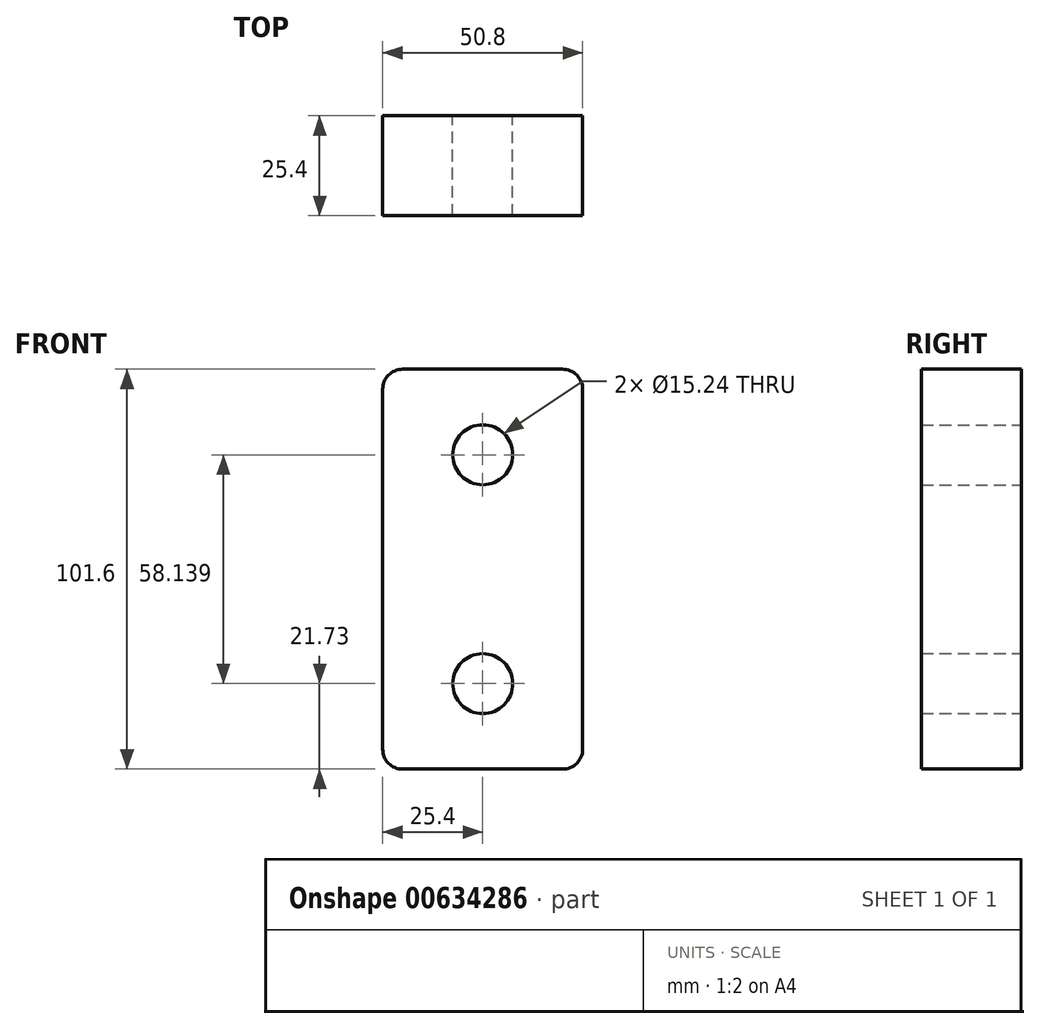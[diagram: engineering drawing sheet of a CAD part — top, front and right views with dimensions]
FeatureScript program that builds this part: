
annotation { "Feature Type Name" : "Feature", "Feature Type Description" : "" }
export const myFeature = defineFeature(function(context is Context, id is Id, definition is map)
    precondition{}
    {
        {
            var Q0;
            Q0=qCreatedBy(makeId("Front.planeOp"),FACE);
            var sketch = newSketch(context, id + "F0", { "sketchPlane" : qUnion([Q0])});
            skLineSegment(sketch, "E0.bottom", {"start": v(25.4, -50.8) * mm, "end": v(-25.4, -50.8) * mm});
            skLineSegment(sketch, "E0.top", {"start": v(25.4, 50.8) * mm, "end": v(-25.4, 50.8) * mm});
            skLineSegment(sketch, "E0.left", {"start": v(25.4, -50.8) * mm, "end": v(25.4, 50.8) * mm});
            skLineSegment(sketch, "E0.right", {"start": v(-25.4, -50.8) * mm, "end": v(-25.4, 50.8) * mm});
            skPoint(sketch, "E0.middle", {"position": v(0, 0) * mm});
            skCircle(sketch, "E1", {"center": v(0, -29.07) * mm, "radius": 7.62 * mm});
            skCircle(sketch, "E2.MirrorC", {"center": v(0, 29.07) * mm, "radius": 7.62 * mm});
            skSolve(sketch);
        }
        {
            var Q0;
            Q0=makeQuery(id+"F0.imprint","IMPRINT",FACE,{"disambiguationData":[TD([[makeQuery(id+"F0.imprint","IMPRINT",EDGE,{"derivedFrom":sQuery(id+"F0.wireOp",EDGE,"E0.bottom")}),-1.0]])]});
            extrude(context, id + "F1", {"entities" : qUnion([Q0]), "endBound" : BoundingType.SYMMETRIC, "depth" : 25.4 * mm, "offsetDistance" : 25.4 * mm});
        }
        {
            var Q0;
            Q0=makeQuery(id+"F1.opExtrude","SWEPT_EDGE",EDGE,{"disambiguationData":[OSD([sQuery(id+"F0.wireOp",EDGE,"E0.top"),sQuery(id+"F0.wireOp",EDGE,"E0.left")])]});
            var Q1;
            Q1=makeQuery(id+"F1.opExtrude","SWEPT_EDGE",EDGE,{"disambiguationData":[OSD([sQuery(id+"F0.wireOp",EDGE,"E0.top"),sQuery(id+"F0.wireOp",EDGE,"E0.right")])]});
            var Q2;
            Q2=makeQuery(id+"F1.opExtrude","SWEPT_EDGE",EDGE,{"disambiguationData":[OSD([sQuery(id+"F0.wireOp",EDGE,"E0.bottom"),sQuery(id+"F0.wireOp",EDGE,"E0.left")])]});
            var Q3;
            Q3=makeQuery(id+"F1.opExtrude","SWEPT_EDGE",EDGE,{"disambiguationData":[OSD([sQuery(id+"F0.wireOp",EDGE,"E0.bottom"),sQuery(id+"F0.wireOp",EDGE,"E0.right")])]});
            fillet(context, id + "F2", {"entities" : qUnion([Q0, Q1, Q2, Q3]), "radius" : 5.08 * mm, "tangentPropagation" : true, "allowEdgeOverflow" : false});
        }
    });
